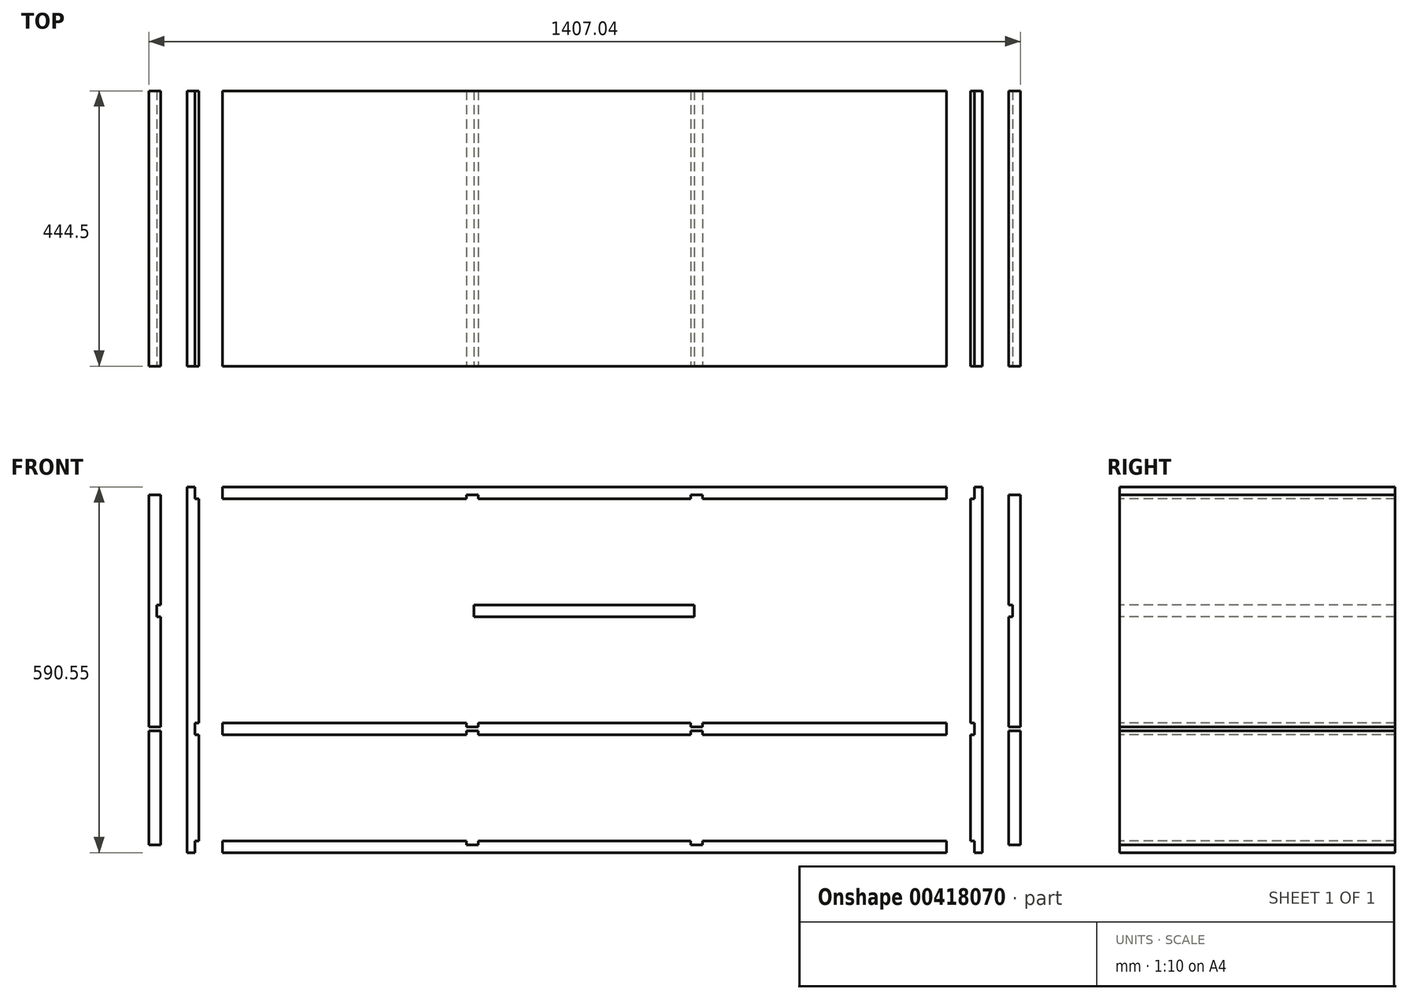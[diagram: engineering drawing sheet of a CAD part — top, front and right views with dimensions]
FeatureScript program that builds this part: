
annotation { "Feature Type Name" : "Feature", "Feature Type Description" : "" }
export const myFeature = defineFeature(function(context is Context, id is Id, definition is map)
    precondition{}
    {
        {
            var Q0;
            Q0=qCreatedBy(makeId("Front.planeOp"),FACE);
            var sketch = newSketch(context, id + "F0", { "sketchPlane" : qUnion([Q0])});
            skLineSegment(sketch, "E0.bottom", {"start": v(-584.2, 219.38) * mm, "end": v(584.2, 219.38) * mm});
            skLineSegment(sketch, "E0.top", {"start": v(-584.2, 200.33) * mm, "end": v(-190.5, 200.33) * mm});
            skLineSegment(sketch, "E0.left", {"start": v(-584.2, 219.38) * mm, "end": v(-584.2, 200.33) * mm});
            skLineSegment(sketch, "E0.right", {"start": v(584.2, 219.38) * mm, "end": v(584.2, 200.33) * mm});
            skLineSegment(sketch, "E1.bottom", {"start": v(-584.2, -180.67) * mm, "end": v(-190.5, -180.67) * mm});
            skLineSegment(sketch, "E1.top", {"start": v(-584.2, -161.62) * mm, "end": v(-190.5, -161.62) * mm});
            skLineSegment(sketch, "E1.left", {"start": v(-584.2, -180.67) * mm, "end": v(-584.2, -161.62) * mm});
            skLineSegment(sketch, "E1.right", {"start": v(584.2, -180.67) * mm, "end": v(584.2, -161.62) * mm});
            skLineSegment(sketch, "E2.bottom", {"start": v(-584.2, -352.12) * mm, "end": v(-190.5, -352.12) * mm});
            skLineSegment(sketch, "E2.top", {"start": v(-584.2, -371.17) * mm, "end": v(584.2, -371.17) * mm});
            skLineSegment(sketch, "E2.left", {"start": v(-584.2, -352.12) * mm, "end": v(-584.2, -371.17) * mm});
            skLineSegment(sketch, "E2.right", {"start": v(584.2, -352.12) * mm, "end": v(584.2, -371.17) * mm});
            skLineSegment(sketch, "E3.bottom", {"start": v(-641.75, 219.38) * mm, "end": v(-629.05, 219.38) * mm});
            skLineSegment(sketch, "E3.top", {"start": v(-641.75, -371.17) * mm, "end": v(-629.05, -371.17) * mm});
            skLineSegment(sketch, "E3.left", {"start": v(-641.75, 219.38) * mm, "end": v(-641.75, -371.17) * mm});
            skLineSegment(sketch, "E3.right", {"start": v(-622.7, 200.33) * mm, "end": v(-622.7, -161.62) * mm});
            skLineSegment(sketch, "E4", {"start": v(-622.7, 200.33) * mm, "end": v(-629.05, 200.33) * mm});
            skLineSegment(sketch, "E5", {"start": v(-629.05, 200.33) * mm, "end": v(-629.05, 219.38) * mm});
            skLineSegment(sketch, "E6", {"start": v(-622.7, -161.62) * mm, "end": v(-629.05, -161.62) * mm});
            skPoint(sketch, "E6.startSnap0", {"position": v(-622.7, -175.6) * mm});
            skLineSegment(sketch, "E7", {"start": v(-629.05, -161.62) * mm, "end": v(-629.05, -180.67) * mm});
            skLineSegment(sketch, "E8", {"start": v(-629.05, -180.67) * mm, "end": v(-622.7, -180.67) * mm});
            skLineSegment(sketch, "E9.trimOffspring", {"start": v(-622.7, -180.67) * mm, "end": v(-622.7, -352.12) * mm});
            skLineSegment(sketch, "E10", {"start": v(-622.7, -352.12) * mm, "end": v(-629.05, -352.12) * mm});
            skLineSegment(sketch, "E11", {"start": v(-629.05, -352.12) * mm, "end": v(-629.05, -371.17) * mm});
            skLineSegment(sketch, "E12.MirrorCS", {"start": v(622.7, -161.62) * mm, "end": v(629.05, -161.62) * mm});
            skLineSegment(sketch, "E13.MirrorCS", {"start": v(629.05, -161.62) * mm, "end": v(629.05, -180.67) * mm});
            skLineSegment(sketch, "E14.MirrorCS", {"start": v(641.75, -371.17) * mm, "end": v(629.05, -371.17) * mm});
            skLineSegment(sketch, "E15.MirrorCS", {"start": v(629.05, 200.33) * mm, "end": v(629.05, 219.38) * mm});
            skLineSegment(sketch, "E16.MirrorCS", {"start": v(622.7, 200.33) * mm, "end": v(629.05, 200.33) * mm});
            skLineSegment(sketch, "E17.MirrorCS", {"start": v(629.05, -180.67) * mm, "end": v(622.7, -180.67) * mm});
            skLineSegment(sketch, "E18.MirrorCS", {"start": v(622.7, -352.12) * mm, "end": v(629.05, -352.12) * mm});
            skLineSegment(sketch, "E19.MirrorCS", {"start": v(641.75, 219.38) * mm, "end": v(629.05, 219.38) * mm});
            skLineSegment(sketch, "E20.MirrorCS", {"start": v(629.05, -352.12) * mm, "end": v(629.05, -371.17) * mm});
            skLineSegment(sketch, "E21.MirrorCS", {"start": v(622.7, -180.67) * mm, "end": v(622.7, -352.12) * mm});
            skLineSegment(sketch, "E22.MirrorCS", {"start": v(641.75, 219.38) * mm, "end": v(641.75, -371.17) * mm});
            skLineSegment(sketch, "E23.MirrorCS", {"start": v(622.7, 200.33) * mm, "end": v(622.7, -161.62) * mm});
            skPoint(sketch, "E24.MirrorP", {"position": v(622.7, -175.6) * mm});
            skLineSegment(sketch, "E25.bottom", {"start": v(-190.5, 206.68) * mm, "end": v(-171.45, 206.68) * mm});
            skLineSegment(sketch, "E25.top", {"start": v(-190.5, -167.97) * mm, "end": v(-171.45, -167.97) * mm});
            skLineSegment(sketch, "E25.left", {"start": v(-190.5, 206.68) * mm, "end": v(-190.5, 200.33) * mm});
            skLineSegment(sketch, "E25.right", {"start": v(-171.45, 206.68) * mm, "end": v(-171.45, 200.33) * mm});
            skLineSegment(sketch, "E26.bottom", {"start": v(-190.5, -174.32) * mm, "end": v(-171.45, -174.32) * mm});
            skLineSegment(sketch, "E26.top", {"start": v(-190.5, -358.47) * mm, "end": v(-171.45, -358.47) * mm});
            skLineSegment(sketch, "E26.left", {"start": v(-190.5, -174.32) * mm, "end": v(-190.5, -180.67) * mm});
            skLineSegment(sketch, "E26.right", {"start": v(-171.45, -174.32) * mm, "end": v(-171.45, -180.67) * mm});
            skLineSegment(sketch, "E27.trimOffspring", {"start": v(-171.45, -161.62) * mm, "end": v(171.45, -161.62) * mm});
            skLineSegment(sketch, "E28.trimOffspring", {"start": v(-171.45, -352.12) * mm, "end": v(171.45, -352.12) * mm});
            skLineSegment(sketch, "E29.trimOffspring", {"start": v(-171.45, 200.33) * mm, "end": v(171.45, 200.33) * mm});
            skLineSegment(sketch, "E30.trimOffspring", {"start": v(-171.45, -180.67) * mm, "end": v(171.45, -180.67) * mm});
            skLineSegment(sketch, "E31.MirrorCS", {"start": v(190.5, -174.32) * mm, "end": v(171.45, -174.32) * mm});
            skLineSegment(sketch, "E32.MirrorCS", {"start": v(190.5, -174.32) * mm, "end": v(190.5, -180.67) * mm});
            skLineSegment(sketch, "E33.MirrorCS", {"start": v(190.5, 206.68) * mm, "end": v(171.45, 206.68) * mm});
            skLineSegment(sketch, "E34.MirrorCS", {"start": v(190.5, -358.47) * mm, "end": v(171.45, -358.47) * mm});
            skLineSegment(sketch, "E35.MirrorCS", {"start": v(190.5, 206.68) * mm, "end": v(190.5, 200.33) * mm});
            skLineSegment(sketch, "E36.MirrorCS", {"start": v(190.5, -167.97) * mm, "end": v(171.45, -167.97) * mm});
            skLineSegment(sketch, "E37.MirrorCS", {"start": v(171.45, -174.32) * mm, "end": v(171.45, -180.67) * mm});
            skLineSegment(sketch, "E38.MirrorCS", {"start": v(171.45, 206.68) * mm, "end": v(171.45, 200.33) * mm});
            skLineSegment(sketch, "E39.trimOffspring", {"start": v(-171.45, -161.62) * mm, "end": v(-171.45, -167.97) * mm});
            skLineSegment(sketch, "E40.trimOffspring", {"start": v(-190.5, -161.62) * mm, "end": v(-190.5, -167.97) * mm});
            skLineSegment(sketch, "E41.trimOffspring", {"start": v(-171.45, -352.12) * mm, "end": v(-171.45, -358.47) * mm});
            skLineSegment(sketch, "E42.trimOffspring", {"start": v(-190.5, -352.12) * mm, "end": v(-190.5, -358.47) * mm});
            skLineSegment(sketch, "E43.trimOffspring", {"start": v(171.45, -352.12) * mm, "end": v(171.45, -358.47) * mm});
            skLineSegment(sketch, "E44.trimOffspring", {"start": v(190.5, -352.12) * mm, "end": v(190.5, -358.47) * mm});
            skLineSegment(sketch, "E45.trimOffspring", {"start": v(190.5, -180.67) * mm, "end": v(584.2, -180.67) * mm});
            skLineSegment(sketch, "E46.trimOffspring", {"start": v(190.5, -161.62) * mm, "end": v(190.5, -167.97) * mm});
            skLineSegment(sketch, "E47.trimOffspring", {"start": v(171.45, -161.62) * mm, "end": v(171.45, -167.97) * mm});
            skLineSegment(sketch, "E48.trimOffspring", {"start": v(190.5, -352.12) * mm, "end": v(584.2, -352.12) * mm});
            skLineSegment(sketch, "E49.trimOffspring", {"start": v(190.5, -161.62) * mm, "end": v(584.2, -161.62) * mm});
            skLineSegment(sketch, "E50.trimOffspring", {"start": v(190.5, 200.33) * mm, "end": v(584.2, 200.33) * mm});
            skLineSegment(sketch, "E51.bottom", {"start": v(702.98, 206.68) * mm, "end": v(683.93, 206.68) * mm});
            skLineSegment(sketch, "E51.top", {"start": v(702.98, -167.97) * mm, "end": v(683.93, -167.97) * mm});
            skLineSegment(sketch, "E51.left", {"start": v(702.98, 206.68) * mm, "end": v(702.98, -167.97) * mm});
            skLineSegment(sketch, "E51.right", {"start": v(683.93, 206.68) * mm, "end": v(683.93, 28.88) * mm});
            skLineSegment(sketch, "E52.bottom", {"start": v(683.93, -174.32) * mm, "end": v(703.52, -174.32) * mm});
            skLineSegment(sketch, "E52.top", {"start": v(683.93, -358.47) * mm, "end": v(703.52, -358.47) * mm});
            skLineSegment(sketch, "E52.left", {"start": v(683.93, -174.32) * mm, "end": v(683.93, -358.47) * mm});
            skLineSegment(sketch, "E52.right", {"start": v(703.52, -174.32) * mm, "end": v(703.52, -358.47) * mm});
            skLineSegment(sketch, "E53", {"start": v(683.93, 28.88) * mm, "end": v(690.28, 28.88) * mm});
            skLineSegment(sketch, "E54", {"start": v(690.28, 28.88) * mm, "end": v(690.28, 9.83) * mm});
            skLineSegment(sketch, "E55", {"start": v(683.93, 9.83) * mm, "end": v(690.28, 9.83) * mm});
            skLineSegment(sketch, "E56.trimOffspring", {"start": v(683.93, 9.83) * mm, "end": v(683.93, -167.97) * mm});
            skLineSegment(sketch, "E57.MirrorCS", {"start": v(-683.93, -358.47) * mm, "end": v(-703.52, -358.47) * mm});
            skLineSegment(sketch, "E58.MirrorCS", {"start": v(-683.93, -174.32) * mm, "end": v(-703.52, -174.32) * mm});
            skLineSegment(sketch, "E59.MirrorCS", {"start": v(-702.98, -167.97) * mm, "end": v(-683.93, -167.97) * mm});
            skLineSegment(sketch, "E60.MirrorCS", {"start": v(-683.93, 9.83) * mm, "end": v(-690.28, 9.83) * mm});
            skLineSegment(sketch, "E61.MirrorCS", {"start": v(-683.93, 28.88) * mm, "end": v(-690.28, 28.88) * mm});
            skLineSegment(sketch, "E62.MirrorCS", {"start": v(-702.98, 206.68) * mm, "end": v(-683.93, 206.68) * mm});
            skLineSegment(sketch, "E63.MirrorCS", {"start": v(-690.28, 28.88) * mm, "end": v(-690.28, 9.83) * mm});
            skLineSegment(sketch, "E64.MirrorCS", {"start": v(-683.93, -174.32) * mm, "end": v(-683.93, -358.47) * mm});
            skLineSegment(sketch, "E65.MirrorCS", {"start": v(-683.93, 206.68) * mm, "end": v(-683.93, 28.88) * mm});
            skLineSegment(sketch, "E66.MirrorCS", {"start": v(-702.98, 206.68) * mm, "end": v(-702.98, -167.97) * mm});
            skLineSegment(sketch, "E67.MirrorCS", {"start": v(-683.93, 9.83) * mm, "end": v(-683.93, -167.97) * mm});
            skLineSegment(sketch, "E68.MirrorCS", {"start": v(-703.52, -174.32) * mm, "end": v(-703.52, -358.47) * mm});
            skPoint(sketch, "E69.firstSnap0", {"position": v(-180.97, -167.97) * mm});
            skPoint(sketch, "E69.oppositeSnap0", {"position": v(180.97, -167.97) * mm});
            skLineSegment(sketch, "E69.bottom", {"start": v(-178.45, 28.88) * mm, "end": v(177.15, 28.88) * mm});
            skLineSegment(sketch, "E69.top", {"start": v(-178.45, 9.83) * mm, "end": v(177.15, 9.83) * mm});
            skLineSegment(sketch, "E69.left", {"start": v(-178.45, 28.88) * mm, "end": v(-178.45, 9.83) * mm});
            skLineSegment(sketch, "E69.right", {"start": v(177.15, 28.88) * mm, "end": v(177.15, 9.83) * mm});
            skSolve(sketch);
        }
        {
            var Q0;
            Q0=makeQuery(id+"F0.imprint","IMPRINT",FACE,{"disambiguationData":[TD([[makeQuery(id+"F0.imprint","IMPRINT",EDGE,{"derivedFrom":sQuery(id+"F0.wireOp",EDGE,"E3.bottom")}),-1.0]])]});
            var Q1;
            Q1=makeQuery(id+"F0.imprint","IMPRINT",FACE,{"disambiguationData":[TD([[makeQuery(id+"F0.imprint","IMPRINT",EDGE,{"derivedFrom":sQuery(id+"F0.wireOp",EDGE,"E2.bottom")}),-1.0]])]});
            var Q2;
            Q2=makeQuery(id+"F0.imprint","IMPRINT",FACE,{"disambiguationData":[TD([[makeQuery(id+"F0.imprint","IMPRINT",EDGE,{"derivedFrom":sQuery(id+"F0.wireOp",EDGE,"E12.MirrorCS")}),1.0]])]});
            extrude(context, id + "F1", {"entities" : qUnion([Q0, Q1, Q2]), "oppositeDirection" : true, "depth" : 444.5 * mm});
        }
        {
            var Q0;
            Q0=makeQuery(id+"F0.imprint","IMPRINT",FACE,{"disambiguationData":[TD([[makeQuery(id+"F0.imprint","IMPRINT",EDGE,{"derivedFrom":sQuery(id+"F0.wireOp",EDGE,"E0.bottom")}),-1.0]])]});
            var Q1;
            Q1=makeQuery(id+"F0.imprint","IMPRINT",FACE,{"disambiguationData":[TD([[makeQuery(id+"F0.imprint","IMPRINT",EDGE,{"derivedFrom":sQuery(id+"F0.wireOp",EDGE,"E59.MirrorCS")}),1.0]])]});
            var Q2;
            Q2=makeQuery(id+"F0.imprint","IMPRINT",FACE,{"disambiguationData":[TD([[makeQuery(id+"F0.imprint","IMPRINT",EDGE,{"derivedFrom":sQuery(id+"F0.wireOp",EDGE,"E69.bottom")}),-1.0]])]});
            var Q3;
            Q3=makeQuery(id+"F0.imprint","IMPRINT",FACE,{"disambiguationData":[TD([[makeQuery(id+"F0.imprint","IMPRINT",EDGE,{"derivedFrom":sQuery(id+"F0.wireOp",EDGE,"E57.MirrorCS")}),-1.0]])]});
            var Q4;
            Q4=makeQuery(id+"F0.imprint","IMPRINT",FACE,{"disambiguationData":[TD([[makeQuery(id+"F0.imprint","IMPRINT",EDGE,{"derivedFrom":sQuery(id+"F0.wireOp",EDGE,"E52.bottom")}),-1.0]])]});
            var Q5;
            Q5=makeQuery(id+"F0.imprint","IMPRINT",FACE,{"disambiguationData":[TD([[makeQuery(id+"F0.imprint","IMPRINT",EDGE,{"derivedFrom":sQuery(id+"F0.wireOp",EDGE,"E51.bottom")}),1.0]])]});
            var Q6;
            Q6=makeQuery(id+"F0.imprint","IMPRINT",FACE,{"disambiguationData":[TD([[makeQuery(id+"F0.imprint","IMPRINT",EDGE,{"derivedFrom":sQuery(id+"F0.wireOp",EDGE,"E1.bottom")}),1.0]])]});
            extrude(context, id + "F2", {"entities" : qUnion([Q0, Q1, Q2, Q3, Q4, Q5, Q6]), "oppositeDirection" : true, "depth" : 444.5 * mm});
        }
    });
